# Revit family: 703420001 Fluxometro Orinal Push Tru Flush OC
name_source: partatom
category: Aparatos sanitarios
revit_build: Autodesk Revit 2018 (Build: 20170223_1515(x64)
units: mm (PartAtom-declared; Revit-internal decimal feet)

## family parameters
Anfitrión = Cara
Compartido = No
Corte con vacíos al cargar = No
Cota de conector redondo = Diámetro de uso
Número OmniClass = 23.45.05.14.99
Punto de cálculo de habitación = No
Tipo de pieza = Normal
Título OmniClass = Other Sanitary Washing Plumbing Fixtures

## types (1)
- 703420001 Fluxometro Orinal Push Tru Flush OC
    Accionamiento = Push
    Cauda mínimo de entrada = 76 lpm
    Consumo de agua = 1 lt por descarga
    Cumple ADA = Aplica de acuerdo al tipo de Orinal Porcelana
    Cumple EDGE = Sí
    Cumple LEED = Sí
    Código de montaje = D2010200
    Diámetro de conexión = 1 ½” NPT / Hembra
    Elevación por defecto = 1219 mm
    Faceplate Material = Metal-Sloan-Chrome
    Garantía = 3 años por Defectos de fabricación
1 año por acabados
    Marca = SLOAN
    Material de fabricación = Latón
    Nombre = Fluxometro Orinal Push Tru Flush
    Presión Máxima = 80 Psi
    Presión mínima = 25 Psi
    Referencia = 703420001
    Tipo = Válvula de descarga
    Tráfico = Institucional, alto tráfico
    URL = https://www.corona.co
    Vida util ( ciclos ) = 150000
